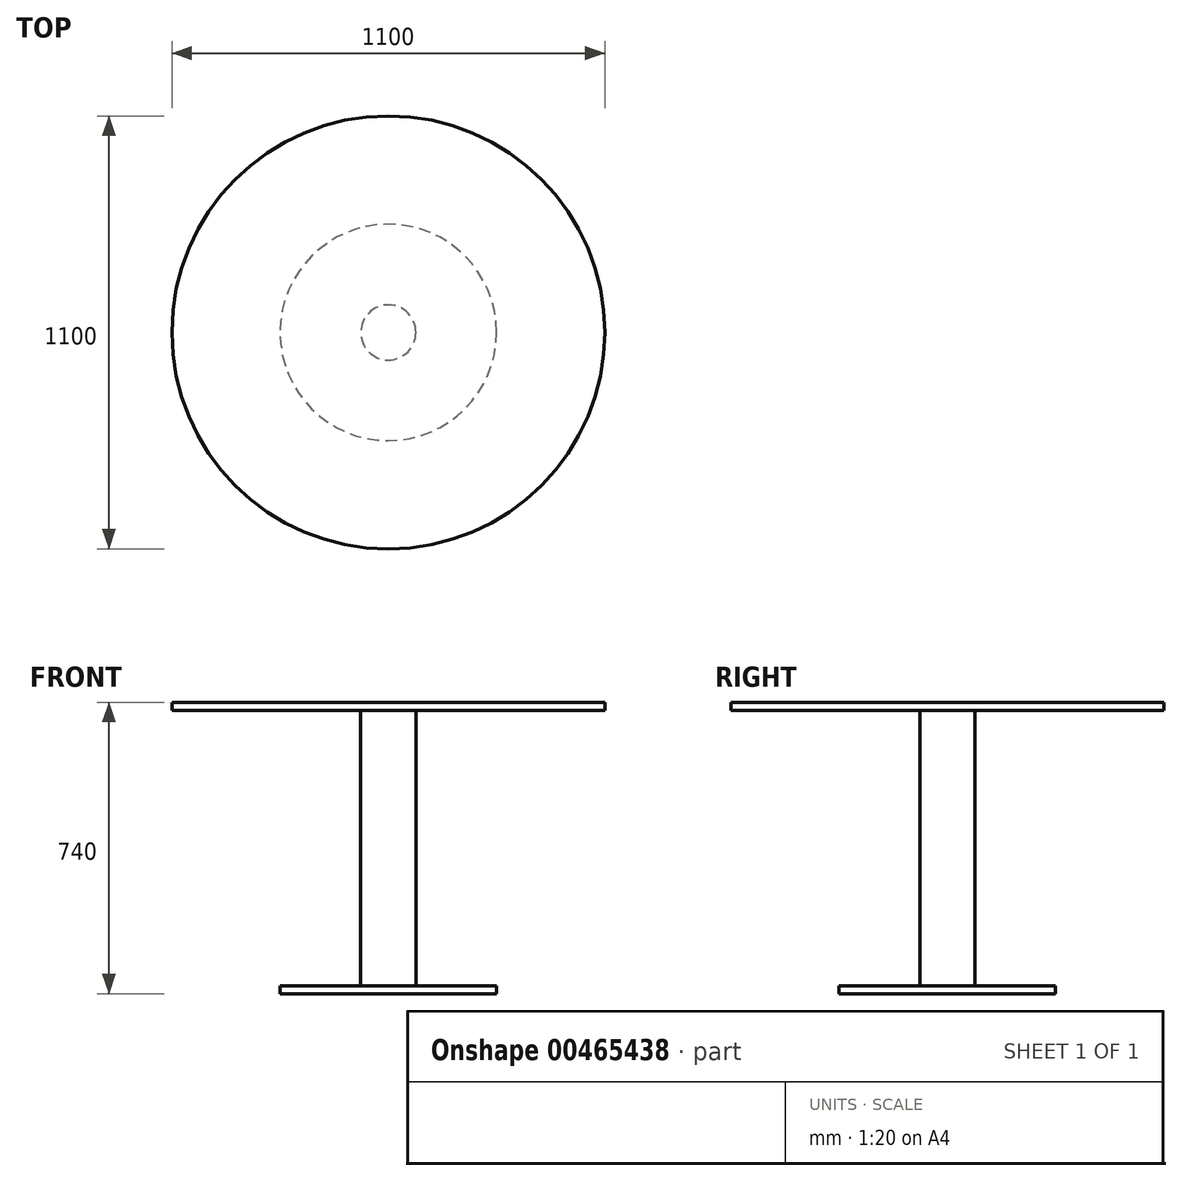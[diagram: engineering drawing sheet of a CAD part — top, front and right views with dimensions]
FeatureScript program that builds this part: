
annotation { "Feature Type Name" : "Feature", "Feature Type Description" : "" }
export const myFeature = defineFeature(function(context is Context, id is Id, definition is map)
    precondition{}
    {
        {
            var Q0;
            Q0=qCreatedBy(makeId("Top.planeOp"),FACE);
            var sketch = newSketch(context, id + "F0", { "sketchPlane" : qUnion([Q0])});
            skCircle(sketch, "E0", {"center": v(0, 0) * mm, "radius": 550 * mm});
            skSolve(sketch);
        }
        {
            var Q0;
            Q0=makeQuery(id+"F0.imprint","IMPRINT",FACE,{"disambiguationData":[TD([[makeQuery(id+"F0.imprint","IMPRINT",EDGE,{"derivedFrom":sQuery(id+"F0.wireOp",EDGE,"E0")}),1.0]])]});
            extrude(context, id + "F1", {"entities" : qUnion([Q0]), "depth" : 20 * mm});
        }
        {
            var Q0;
            Q0=makeQuery(id+"F1.opExtrude","CAP_FACE",FACE,{"disambiguationData":[OSD([sQuery(id+"F0.wireOp",EDGE,"E0")])],"isStart":true});
            var sketch = newSketch(context, id + "F2", { "sketchPlane" : qUnion([Q0])});
            skCircle(sketch, "E1", {"center": v(0, 0) * mm, "radius": 70 * mm});
            skSolve(sketch);
        }
        {
            var Q0;
            Q0=makeQuery(id+"F2.imprint","IMPRINT",FACE,{"disambiguationData":[TD([[makeQuery(id+"F2.imprint","IMPRINT",EDGE,{"derivedFrom":sQuery(id+"F2.wireOp",EDGE,"E1")}),1.0]])]});
            extrude(context, id + "F3", {"entities" : qUnion([Q0]), "depth" : 700 * mm});
        }
        {
            var Q0;
            Q0=makeQuery(id+"F3.opExtrude","CAP_FACE",FACE,{"disambiguationData":[OSD([sQuery(id+"F2.wireOp",EDGE,"E1")])],"isStart":false});
            var sketch = newSketch(context, id + "F4", { "sketchPlane" : qUnion([Q0])});
            skCircle(sketch, "E2", {"center": v(0, 0) * mm, "radius": 275 * mm});
            skSolve(sketch);
        }
        {
            var Q0;
            Q0 = qSketchRegion(id + "F4", true);
            extrude(context, id + "F5", {"entities" : qUnion([Q0]), "operationType" : NewBodyOperationType.ADD, "depth" : 20 * mm});
        }
    });
